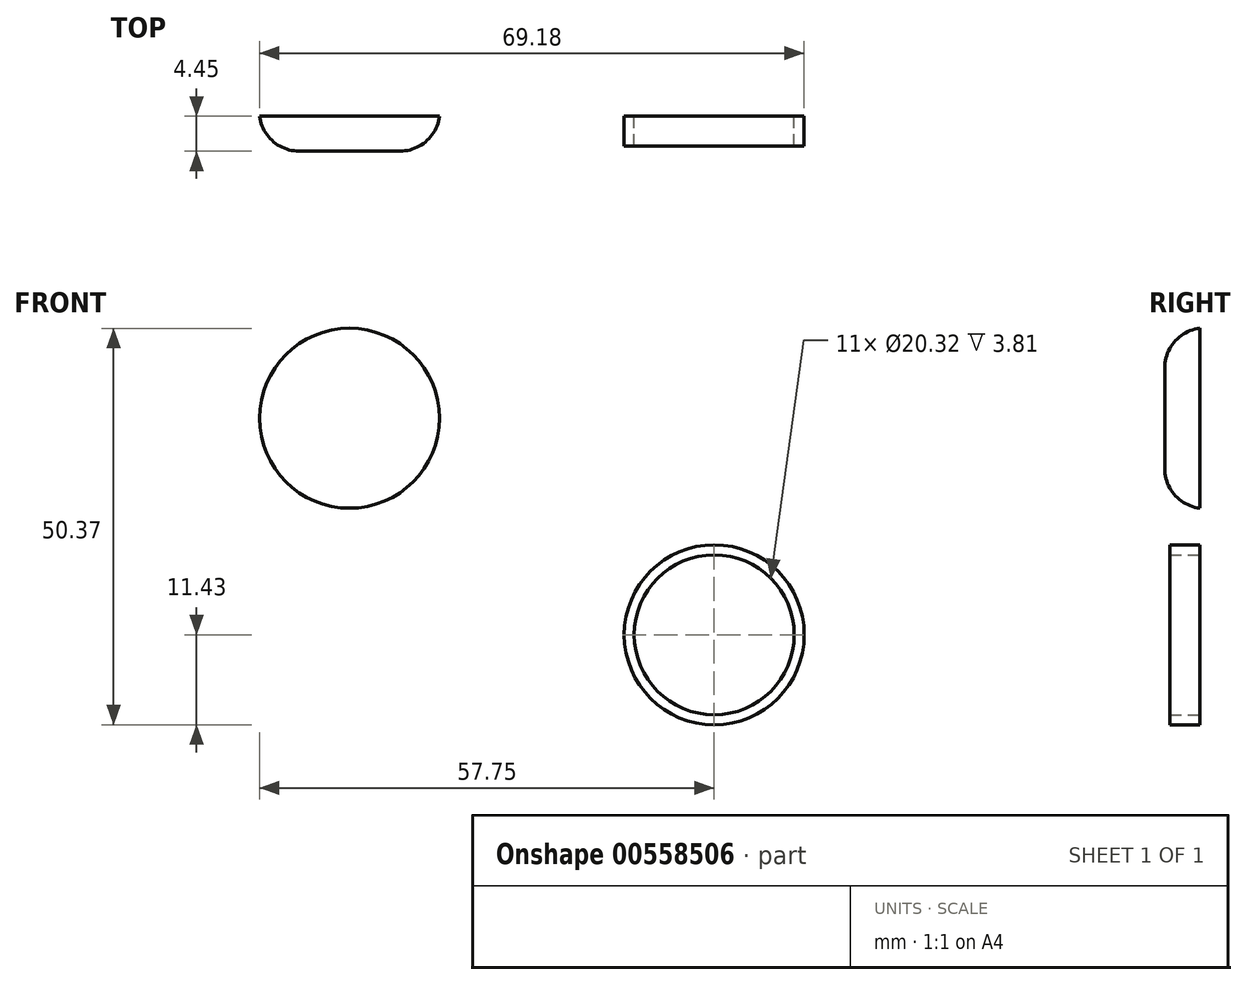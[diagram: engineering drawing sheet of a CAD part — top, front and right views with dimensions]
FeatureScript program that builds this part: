
annotation { "Feature Type Name" : "Feature", "Feature Type Description" : "" }
export const myFeature = defineFeature(function(context is Context, id is Id, definition is map)
    precondition{}
    {
        {
            var Q0;
            Q0=qCreatedBy(makeId("Front.planeOp"),FACE);
            var sketch = newSketch(context, id + "F0", { "sketchPlane" : qUnion([Q0])});
            skCircle(sketch, "E0", {"center": v(0, 0) * mm, "radius": 11.43 * mm});
            skCircle(sketch, "E1", {"center": v(0, 0) * mm, "radius": 10.16 * mm});
            skSolve(sketch);
        }
        {
            var Q0;
            Q0=makeQuery(id+"F0.imprint","IMPRINT",FACE,{"disambiguationData":[TD([[makeQuery(id+"F0.imprint","IMPRINT",EDGE,{"derivedFrom":sQuery(id+"F0.wireOp",EDGE,"E0")}),1.0]])]});
            extrude(context, id + "F1", {"entities" : qUnion([Q0]), "depth" : 3.8 * mm, "offsetDistance" : 25.4 * mm});
        }
        {
            var Q0;
            Q0=qCreatedBy(makeId("Front.planeOp"),FACE);
            var sketch = newSketch(context, id + "F2", { "sketchPlane" : qUnion([Q0])});
            skCircle(sketch, "E2", {"center": v(-46.32, 27.51) * mm, "radius": 11.43 * mm});
            skSolve(sketch);
        }
        {
            var Q0;
            Q0=makeQuery(id+"F2.imprint","IMPRINT",FACE,{"disambiguationData":[TD([[makeQuery(id+"F2.imprint","IMPRINT",EDGE,{"derivedFrom":sQuery(id+"F2.wireOp",EDGE,"E2")}),1.0]])]});
            extrude(context, id + "F3", {"entities" : qUnion([Q0]), "depth" : 4.44 * mm, "offsetDistance" : 25.4 * mm});
        }
        {
            var Q0;
            Q0=makeQuery(id+"F3.opExtrude","CAP_EDGE",EDGE,{"disambiguationData":[OSD([sQuery(id+"F2.wireOp",EDGE,"E2")])],"isStart":false});
            fillet(context, id + "F4", {"entities" : qUnion([Q0]), "radius" : 5.08 * mm, "tangentPropagation" : true, "allowEdgeOverflow" : false});
        }
    });
